FCSTD DOCUMENT  (FreeCAD 0.20R29177 +426 (Git))
Label: espFreeCAd
License: All rights reserved
LicenseURL: http://en.wikipedia.org/wiki/All_rights_reserved
objects: Mesh::Feature×1, PartDesign::CoordinateSystem×1, Part::Feature×1, PartDesign::FeatureBase×1, PartDesign::Body×1
note: 4 computed .brp shape members not serialized (recipe doc carries the construction recipe); baked Part::Feature solids carry a one-line shape summary decoded from their .brp

FEATURE [Mesh::Feature] ESP32_CAM_ESP32CAM_MB  label="ESP32-CAM-ESP32CAM+MB"
FEATURE [PartDesign::CoordinateSystem] LCS_Origin
  AttacherType = Attacher::AttachEngine3D
  MapMode = 2
  Support = -> [X_Axis]
FEATURE [Part::Feature] ESP32_CAM_ESP32CAM_MB001
  shape: large baked B-rep (133 MB .brp); summary skipped
FEATURE [PartDesign::FeatureBase] BaseFeature
  BaseFeature = -> ESP32_CAM_ESP32CAM_MB001
FEATURE [PartDesign::Body] esp
  BaseFeature = -> ESP32_CAM_ESP32CAM_MB001
  Group = -> [BaseFeature,LCS_Origin]
  Origin = -> Origin
  Tip = -> BaseFeature
